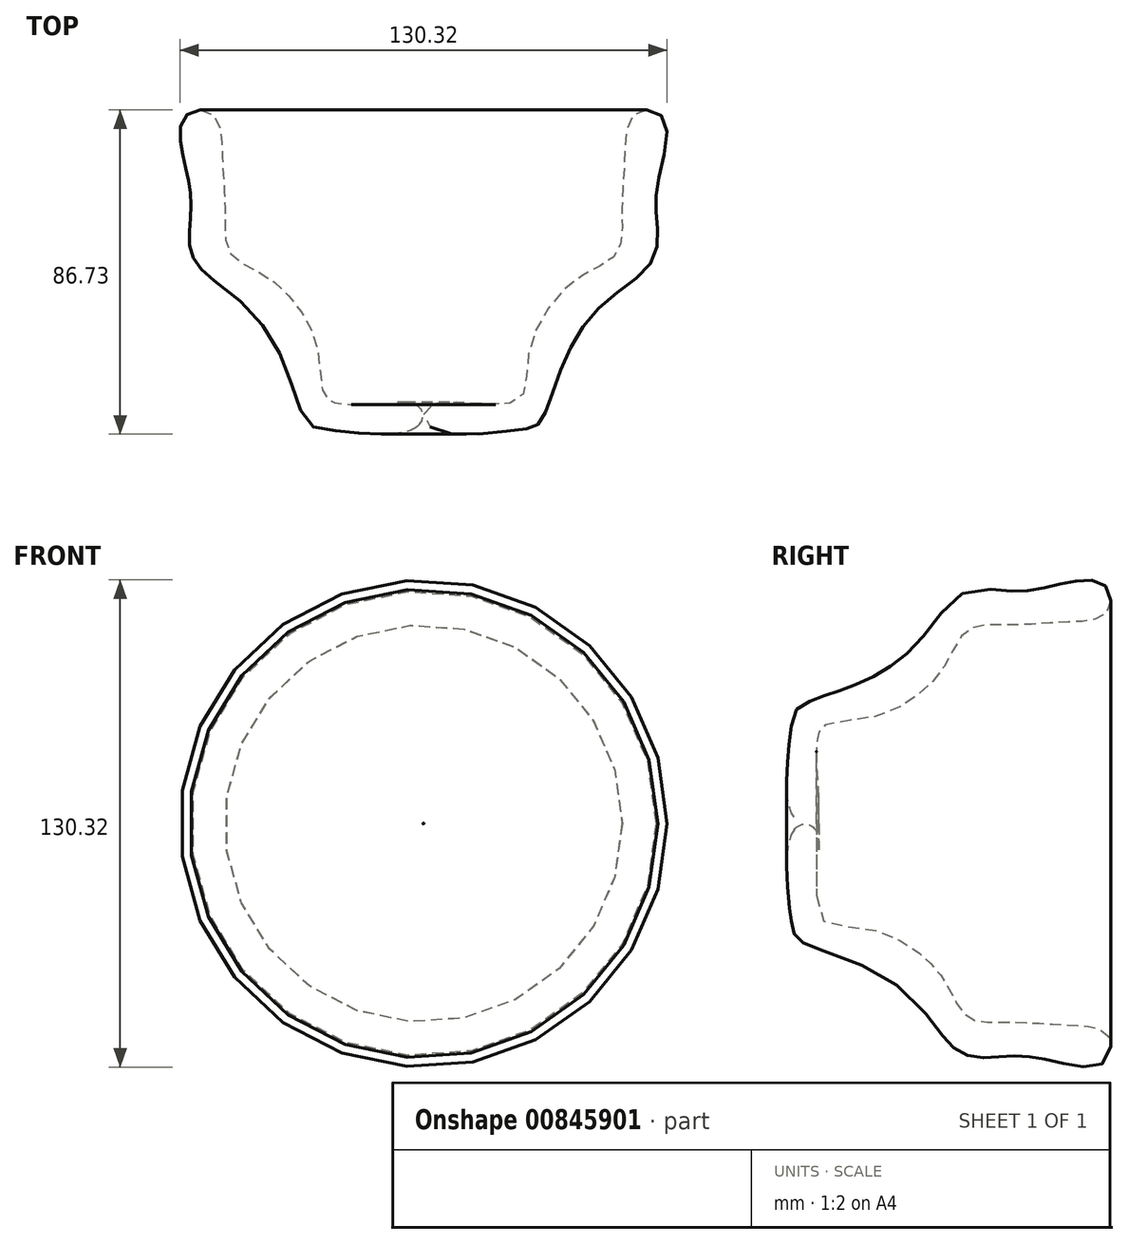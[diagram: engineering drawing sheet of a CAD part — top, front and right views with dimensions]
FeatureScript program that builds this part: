
annotation { "Feature Type Name" : "Feature", "Feature Type Description" : "" }
export const myFeature = defineFeature(function(context is Context, id is Id, definition is map)
    precondition{}
    {
        {
            var Q0;
            Q0=qCreatedBy(makeId("Top.planeOp"),FACE);
            var sketch = newSketch(context, id + "F0", { "sketchPlane" : qUnion([Q0])});
            skLineSegment(sketch, "E0", {"start": v(0, 76.22) * mm, "end": v(0, -76.78) * mm});
            skFitSpline(sketch, "E1", {"points": [v(1.76, -52.39) * mm, v(24.67, -53.3) * mm, v(31.14, -51.1) * mm, v(36.68, -37.05) * mm, v(48.14, -19.5) * mm, v(61.44, -7.48) * mm, v(62.36, 3.6) * mm, v(62.92, 13.95) * mm, v(64.21, 30.21) * mm, v(56.64, 31.5) * mm, v(53.86, 20.42) * mm, v(53.12, 4.9) * mm, v(51.65, -6) * mm, v(40.74, -13.03) * mm, v(28.18, -32.43) * mm, v(24.67, -45.55) * mm, v(1.76, -46.66) * mm, v(1.76, -52.39) * mm]});
            skSolve(sketch);
        }
        {
            var Q0;
            Q0 = qSketchRegion(id + "F0", true);
            var Q1;
            Q1=sQuery(id+"F0.wireOp",EDGE,"E0");
            revolve(context, id + "F1", {"surfaceOperationType" : NewSurfaceOperationType.NEW, "entities" : qUnion([Q0]), "axis" : qUnion([Q1]), "revolveType" : RevolveType.FULL});
        }
    });
